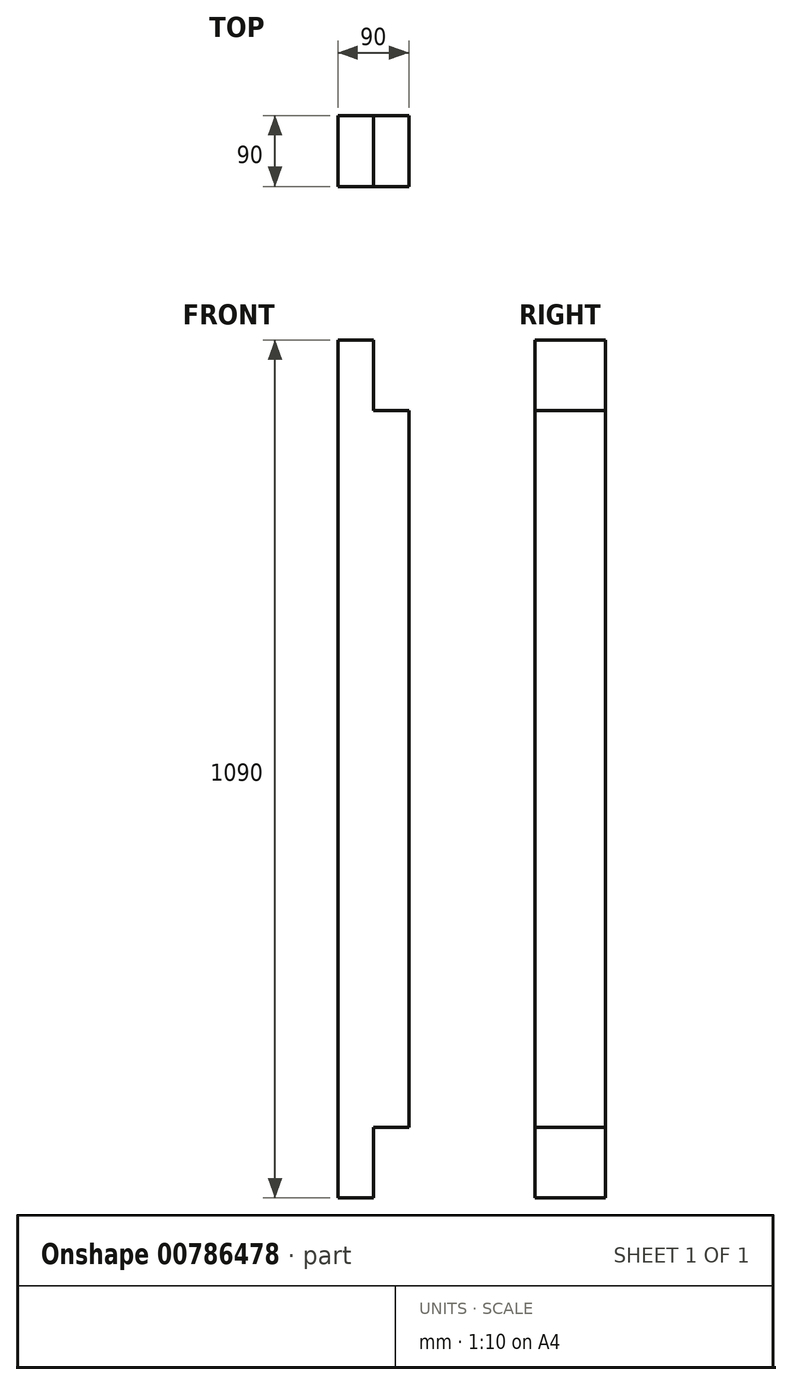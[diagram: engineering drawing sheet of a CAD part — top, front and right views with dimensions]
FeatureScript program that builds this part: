
annotation { "Feature Type Name" : "Feature", "Feature Type Description" : "" }
export const myFeature = defineFeature(function(context is Context, id is Id, definition is map)
    precondition{}
    {
        {
            var Q0;
            Q0=qCreatedBy(makeId("Top.planeOp"),FACE);
            var sketch = newSketch(context, id + "F0", { "sketchPlane" : qUnion([Q0])});
            skLineSegment(sketch, "E0.bottom", {"start": v(-45, 45) * mm, "end": v(45, 45) * mm});
            skLineSegment(sketch, "E0.top", {"start": v(-45, -45) * mm, "end": v(45, -45) * mm});
            skLineSegment(sketch, "E0.left", {"start": v(-45, 45) * mm, "end": v(-45, -45) * mm});
            skLineSegment(sketch, "E0.right", {"start": v(45, 45) * mm, "end": v(45, -45) * mm});
            skSolve(sketch);
        }
        {
            var Q0;
            Q0=makeQuery(id+"F0.imprint","IMPRINT",FACE,{"disambiguationData":[TD([[makeQuery(id+"F0.imprint","IMPRINT",EDGE,{"derivedFrom":sQuery(id+"F0.wireOp",EDGE,"E0.bottom")}),-1.0]])]});
            extrude(context, id + "F1", {"entities" : qUnion([Q0]), "depth" : 1090 * mm, "offsetDistance" : 25 * mm});
        }
        {
            var Q0;
            Q0=makeQuery(id+"F1.opExtrude","SWEPT_FACE",FACE,{"disambiguationData":[OSD([sQuery(id+"F0.wireOp",EDGE,"E0.right")])]});
            var sketch = newSketch(context, id + "F2", { "sketchPlane" : qUnion([Q0])});
            skLineSegment(sketch, "E1.bottom", {"start": v(-45, 1090) * mm, "end": v(45, 1090) * mm});
            skLineSegment(sketch, "E1.top", {"start": v(-45, 1000) * mm, "end": v(45, 1000) * mm});
            skLineSegment(sketch, "E1.left", {"start": v(-45, 1090) * mm, "end": v(-45, 1000) * mm});
            skLineSegment(sketch, "E1.right", {"start": v(45, 1090) * mm, "end": v(45, 1000) * mm});
            skLineSegment(sketch, "E2.bottom", {"start": v(-45, 0) * mm, "end": v(45, 0) * mm});
            skLineSegment(sketch, "E2.top", {"start": v(-45, 89.62) * mm, "end": v(45, 89.62) * mm});
            skLineSegment(sketch, "E2.left", {"start": v(-45, 0) * mm, "end": v(-45, 89.62) * mm});
            skLineSegment(sketch, "E2.right", {"start": v(45, 0) * mm, "end": v(45, 89.62) * mm});
            skSolve(sketch);
        }
        {
            var Q0;
            Q0=makeQuery(id+"F2.imprint","IMPRINT",FACE,{"disambiguationData":[TD([[makeQuery(id+"F2.imprint","IMPRINT",EDGE,{"derivedFrom":sQuery(id+"F2.wireOp",EDGE,"E1.bottom")}),1.0]])]});
            var Q1;
            Q1=makeQuery(id+"F2.imprint","IMPRINT",FACE,{"disambiguationData":[TD([[makeQuery(id+"F2.imprint","IMPRINT",EDGE,{"derivedFrom":sQuery(id+"F2.wireOp",EDGE,"E2.bottom")}),-1.0]])]});
            extrude(context, id + "F3", {"entities" : qUnion([Q0, Q1]), "operationType" : NewBodyOperationType.REMOVE, "oppositeDirection" : true, "depth" : 45 * mm, "offsetDistance" : 25 * mm});
        }
    });
